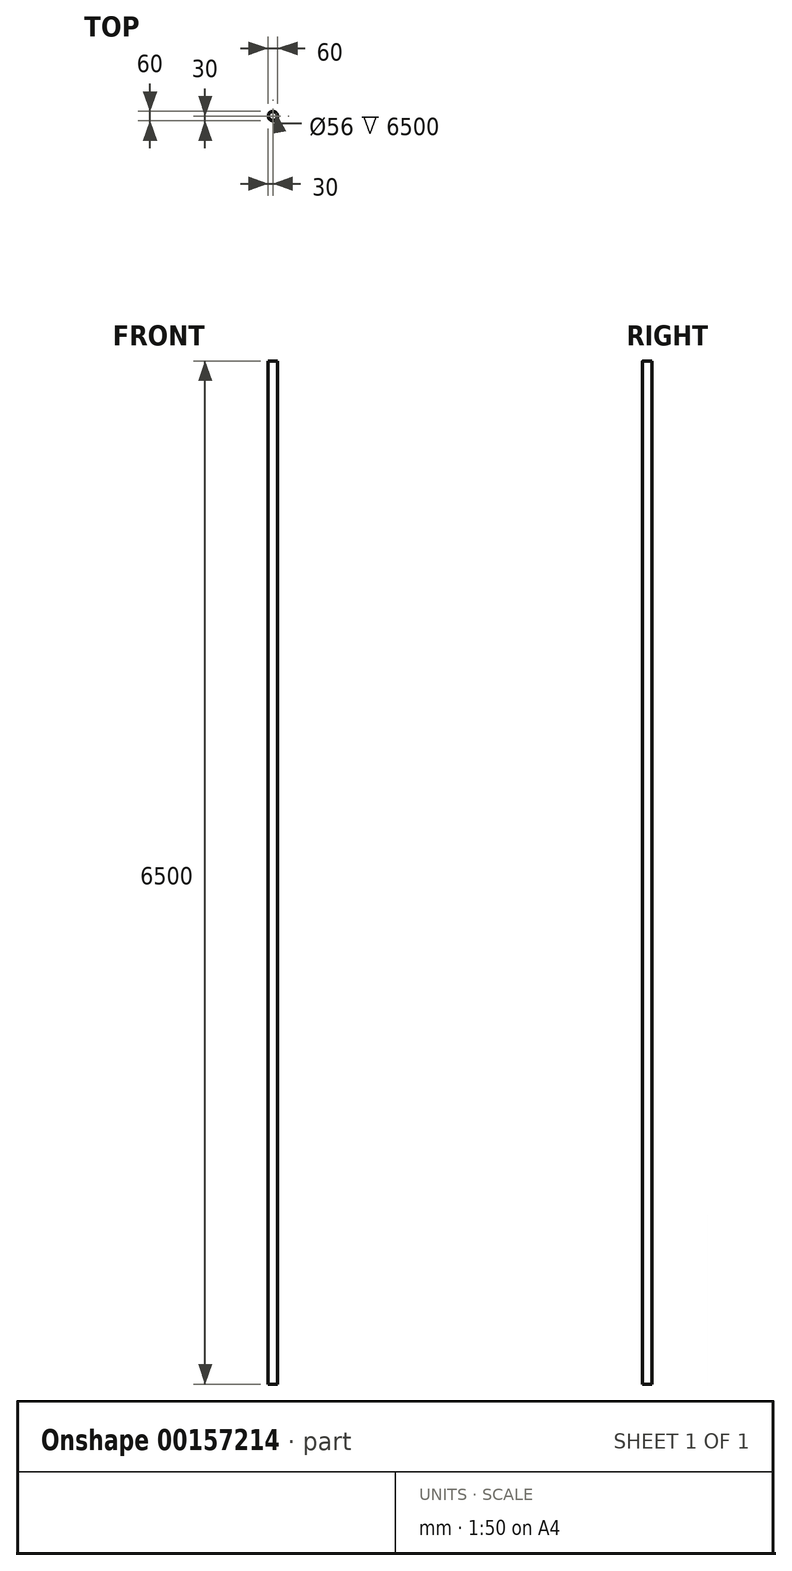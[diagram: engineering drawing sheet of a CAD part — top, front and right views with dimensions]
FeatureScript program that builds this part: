
annotation { "Feature Type Name" : "Feature", "Feature Type Description" : "" }
export const myFeature = defineFeature(function(context is Context, id is Id, definition is map)
    precondition{}
    {
        {
            var Q0;
            Q0=qCreatedBy(makeId("Top.planeOp"),FACE);
            var sketch = newSketch(context, id + "F0", { "sketchPlane" : qUnion([Q0])});
            skCircle(sketch, "E0", {"center": v(0, 0) * mm, "radius": 30 * mm});
            skCircle(sketch, "E1", {"center": v(0, 0) * mm, "radius": 28 * mm});
            skSolve(sketch);
        }
        {
            var Q0;
            Q0=makeQuery(id+"F0.imprint","IMPRINT",FACE,{"disambiguationData":[TD([[makeQuery(id+"F0.imprint","IMPRINT",EDGE,{"derivedFrom":sQuery(id+"F0.wireOp",EDGE,"E0")}),1.0]])]});
            extrude(context, id + "F1", {"entities" : qUnion([Q0]), "depth" : 6500 * mm});
        }
    });
